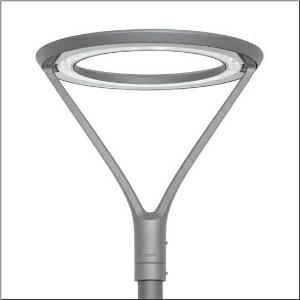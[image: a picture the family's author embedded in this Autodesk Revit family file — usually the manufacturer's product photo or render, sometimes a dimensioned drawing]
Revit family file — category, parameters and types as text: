
# Revit family: dl_r__20___st1_2a_5xa51283wa008p_0b9f
name_source: partatom
category: Lighting Fixtures
units: mm (PartAtom-declared; Revit-internal decimal feet)

## family parameters
Cut with Voids When Loaded = No
Host = Face
Light Source = No
Part Type = Normal
Room Calculation Point = No
Round Connector Dimension = Use Diameter
Shared = No

## types (1)
- --- (1 x LED, 4200 lm, 34.3 W, 3000K)
    Apparent Load = 34 VA
    CIE Flux Codes = 32 72 97 100 100
    Color Rendering = 70
    Color Temperature = 3000K
    Default Elevation = 1800 mm
    Description = DL® 20, mast luminaire, primary light control with reflector, highly specular, primary optical cover: cover, of toughened safety glass of clear glass with excellent transmission level, light distribution: ST1.2a, light emission: direct distribution, primary light characteristic: asymmetric, installation type: post-top, LED, High Power LED, rated luminous flux: 4.180lm, luminous efficacy: 79lm/W, light colour: 730, colour temperature: 3000K, control gear: Plus, control: overheat protection, power reduction, digital communication interface, constant luminous flux control, time-dependent luminous flux control, flexible luminous flux parameterisation, electronic power reduction, mains connection: 230..240V, 50/60Hz, connection cable pre-assembled, cable length: 5m, start of lifetime: 53W, end of service life: 54W, reduction: 24W, luminaire housing, upper part, of cast aluminium, powder-coated, Siteco® metallic grey (DB 702S), diameter: 690mm, height: 690mm, spigot size: 76mm (post-top), mounting height: 4..6m, luminaire housing, of cast aluminium, powder-coated, Siteco® metallic grey (DB 702S), equipment: Power, protection rating (complete): IP66, insulation class (complete): insulation class II (safety insulation), certification: CE, ENEC, VDE, impact resistance: IK08, permissible operating ambient temperature: -25..+30°C, standard-compliant lighting for roads and squares, packaging unit: 1 piece

Light Distribution: ST1.2a
    Height = 690 mm
    Lamp = 1 x LED
    Lamp Light Flux = 4200 lm
    Lamp Power = 34.3 W
    Lamp count = 1
    Length = 690 mm
    Luminous efficacy = 122 lm/W
    Manufacturer = Siteco
    ModVariant = No
    Model = 5XA51283WA008P
    Number of Poles = 1
    OnlyDefault = Yes
    Power Factor = 1
    Product Name = DL® 20 | ST1.2a
    Product group = mast luminaire | pylon top
    ProductGroupID = 6100
    Protection Class = Protection class II
    Protection Degree = IP 66
    RLX_Detail_Level = 1
    RLX_Emergency_Light_Flux = 0 lm
    RLX_Emergency_Type = 0
    RLX_Emergency_Type_DB = No
    RlxData = <blob elided: 206957 chars, md5=f567ca69>
    Socket = socket
    Standby Power = 0 W
    System Light Flux = 4200 lm
    System Power = 34 W
    Type Comments = factory setting: luminous flux: 100 % | dim-lin: 254 | 464 mA
    Type Image = l_1006001.jpg
    URL = http://relux.com
    VarID = @adj_098939
    Voltage = 0 V
    Weight = 0.00 kg
    Width = 0 mm  [stored 0 ft]

note: [stored X ft] marks values corroborated as IEEE doubles in the binary element streams (Revit-internal decimal feet)

## geometry (parser evidence)
native form markers: Blend x4, Sweep x9
no freeform markers — native parametric forms only
